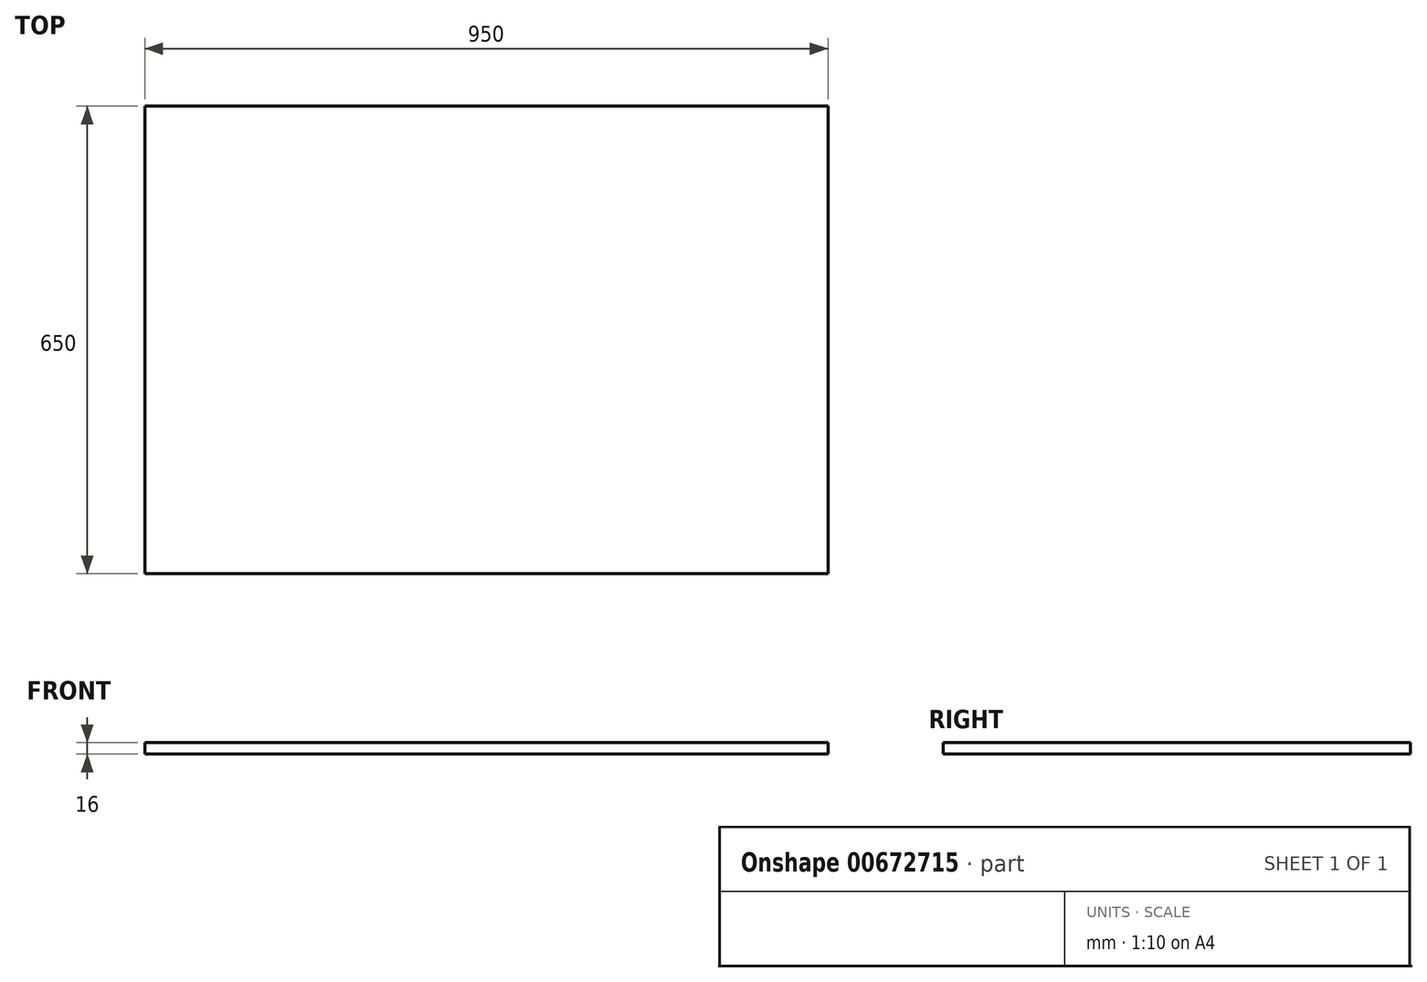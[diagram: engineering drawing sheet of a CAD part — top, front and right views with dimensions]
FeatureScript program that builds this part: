
annotation { "Feature Type Name" : "Feature", "Feature Type Description" : "" }
export const myFeature = defineFeature(function(context is Context, id is Id, definition is map)
    precondition{}
    {
        {
            var Q0;
            Q0=qCreatedBy(makeId("Top.planeOp"),FACE);
            var sketch = newSketch(context, id + "F0", { "sketchPlane" : qUnion([Q0])});
            skLineSegment(sketch, "E0.bottom", {"start": v(0, 0) * mm, "end": v(-950, 0) * mm});
            skLineSegment(sketch, "E0.top", {"start": v(0, 650) * mm, "end": v(-950, 650) * mm});
            skLineSegment(sketch, "E0.left", {"start": v(0, 0) * mm, "end": v(0, 650) * mm});
            skLineSegment(sketch, "E0.right", {"start": v(-950, 0) * mm, "end": v(-950, 650) * mm});
            skSolve(sketch);
        }
        {
            var Q0;
            Q0=makeQuery(id+"F0.imprint","IMPRINT",FACE,{"disambiguationData":[TD([[makeQuery(id+"F0.imprint","IMPRINT",EDGE,{"derivedFrom":sQuery(id+"F0.wireOp",EDGE,"E0.bottom")}),-1.0]])]});
            extrude(context, id + "F1", {"entities" : qUnion([Q0]), "depth" : 16 * mm, "offsetDistance" : 25 * mm});
        }
    });
